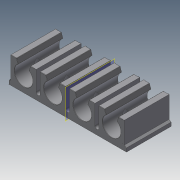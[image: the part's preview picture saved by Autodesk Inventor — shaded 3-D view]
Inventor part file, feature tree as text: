
AUTODESK INVENTOR PART (.ipt)
format: ipt  version: 2020.3 (Build 243373000, 373)  size: 520,704 bytes
history: native  units: in
note: dims shown in document units (in); Inventor stores cm internally (conversion verified against a paired STEP export)
features: extrude x3, sketch x3, pattern_linear x1, plane x1, mirror x1, fillet x1
ambient origin geometry x8: Origin, YZ Plane, XZ Plane, XY Plane, X Axis, Y Axis, Z Axis, Center Point
bodies: Solid1 (feature_tree)
feature tree (10):
  extrude  "Extrusion1"  Depth=1.0in TaperAngle=0.0deg
  extrude  "Extrusion2"  Depth=0.015in
  pattern_linear  "Rectangular Pattern1"  Spacing1=0.02in  [1 undecoded]
  extrude  "Extrusion3"  Depth=1.0in TaperAngle=0.0deg
  plane  "Work Plane1"
  mirror  "Mirror1"
  sketch  "Sketch1"  dims[d0=0.125in d1=1.0in d2=0.0in]
  sketch  "Sketch2"  dims[d3=0.015in d4=0.015in]
  sketch  "Sketch3"  dims[d5=0.1in d6=0.02in d7=1.0in d8=0.0in d9=1.1811in d11=0.4in d12=0.015in d13=1.0in d14=0.0in]
  fillet  "Fillet1"  Radius=1.1811in
note: 1 required parameter value undecoded (feature->parameter linkage not recoverable at this tier; creation-order binding heuristic only, values carry confidence <= 0.55)
